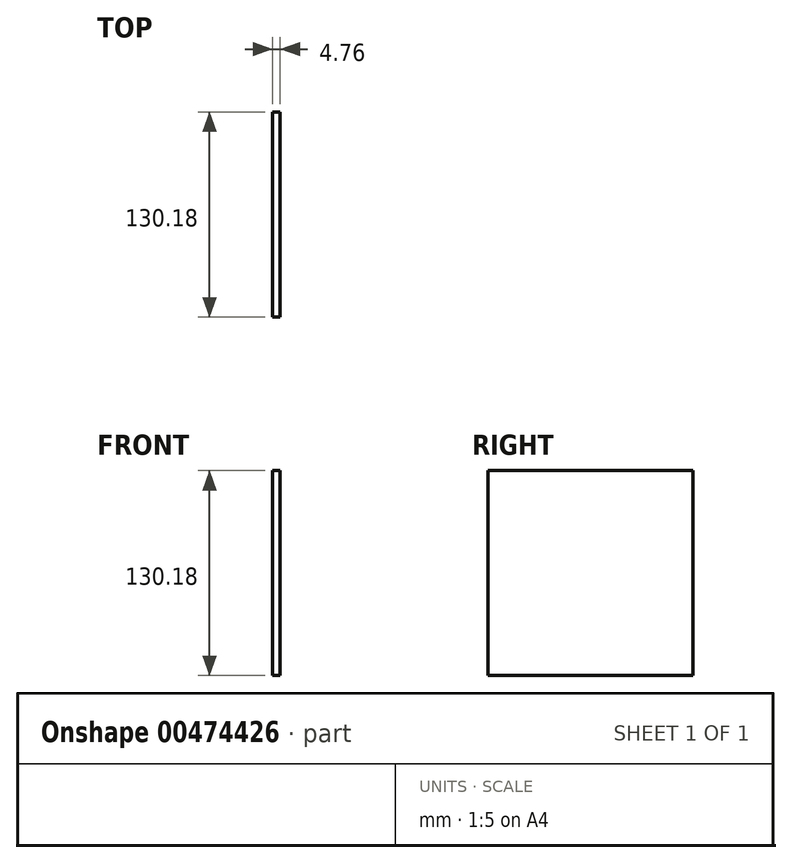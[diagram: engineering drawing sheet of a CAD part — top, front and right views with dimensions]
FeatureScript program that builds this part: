
annotation { "Feature Type Name" : "Feature", "Feature Type Description" : "" }
export const myFeature = defineFeature(function(context is Context, id is Id, definition is map)
    precondition{}
    {
        {
            var Q0;
            Q0=qCreatedBy(makeId("Right.planeOp"),FACE);
            var sketch = newSketch(context, id + "F0", { "sketchPlane" : qUnion([Q0])});
            skLineSegment(sketch, "E0.bottom", {"start": v(-65.09, -65.09) * mm, "end": v(65.09, -65.09) * mm});
            skLineSegment(sketch, "E0.top", {"start": v(-65.09, 65.09) * mm, "end": v(65.09, 65.09) * mm});
            skLineSegment(sketch, "E0.left", {"start": v(-65.09, -65.09) * mm, "end": v(-65.09, 65.09) * mm});
            skLineSegment(sketch, "E0.right", {"start": v(65.09, -65.09) * mm, "end": v(65.09, 65.09) * mm});
            skPoint(sketch, "E0.middle", {"position": v(0, 0) * mm});
            skSolve(sketch);
        }
        {
            var Q0;
            Q0 = qSketchRegion(id + "F0", true);
            extrude(context, id + "F1", {"entities" : qUnion([Q0]), "depth" : 4.76 * mm});
        }
    });
